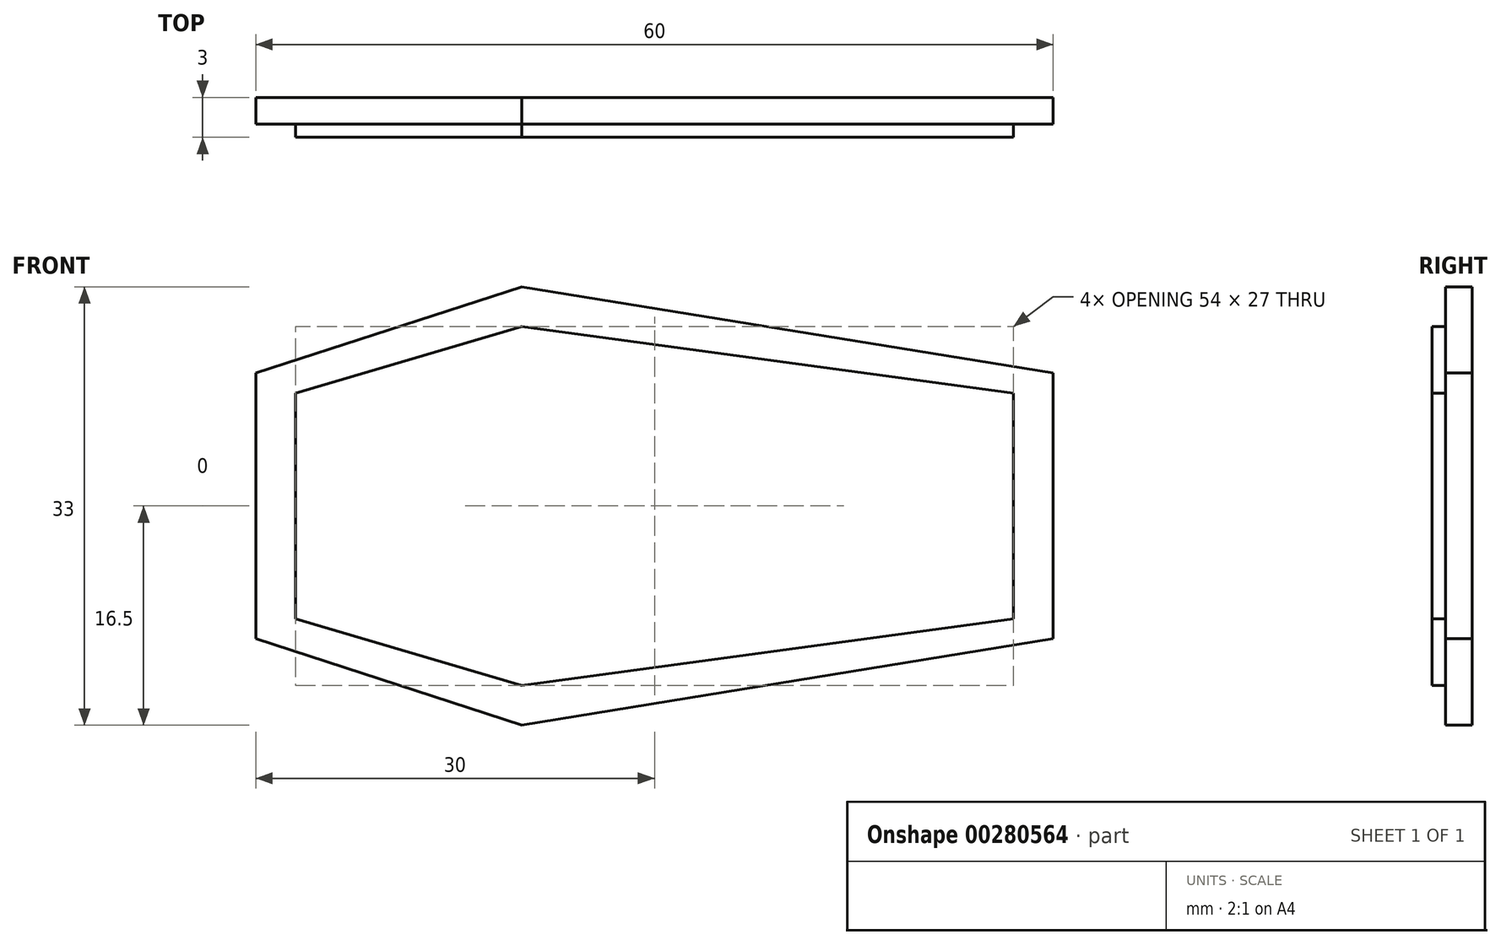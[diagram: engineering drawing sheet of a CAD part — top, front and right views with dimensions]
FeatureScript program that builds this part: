
annotation { "Feature Type Name" : "Feature", "Feature Type Description" : "" }
export const myFeature = defineFeature(function(context is Context, id is Id, definition is map)
    precondition{}
    {
        {
            var Q0;
            Q0=qCreatedBy(makeId("Front.planeOp"),FACE);
            var sketch = newSketch(context, id + "F0", { "sketchPlane" : qUnion([Q0])});
            skLineSegment(sketch, "E0.bottom", {"start": v(30, -10) * mm, "end": v(-30, -10) * mm});
            skLineSegment(sketch, "E0.top", {"start": v(30, 10) * mm, "end": v(-30, 10) * mm});
            skLineSegment(sketch, "E0.left", {"start": v(30, -10) * mm, "end": v(30, 10) * mm});
            skLineSegment(sketch, "E0.right", {"start": v(-30, -10) * mm, "end": v(-30, 10) * mm});
            skPoint(sketch, "E0.middle", {"position": v(0, 0) * mm});
            skPoint(sketch, "E1", {"position": v(-10, 16.5) * mm});
            skPoint(sketch, "E2", {"position": v(-10, -16.5) * mm});
            skLineSegment(sketch, "E3", {"start": v(-10, 16.5) * mm, "end": v(-10, -16.5) * mm});
            skLineSegment(sketch, "E4", {"start": v(-30, -10) * mm, "end": v(-10, -16.5) * mm});
            skLineSegment(sketch, "E5", {"start": v(-30, 10) * mm, "end": v(-10, 16.5) * mm});
            skLineSegment(sketch, "E6", {"start": v(30, 10) * mm, "end": v(-10, 16.5) * mm});
            skLineSegment(sketch, "E7", {"start": v(-10, -16.5) * mm, "end": v(30, -10) * mm});
            skSolve(sketch);
        }
        {
            var Q0;
            {var subQ0=sQuery(id+"F0.wireOp",EDGE,"E0.right");Q0=makeQuery(id+"F0.imprint","IMPRINT",FACE,{"disambiguationData":[TD([[makeQuery(id+"F0.imprint","IMPRINT",EDGE,{"derivedFrom":subQ0}),-1.0]])]});}
            var Q1;
            {var subQ0=sQuery(id+"F0.wireOp",EDGE,"E5");Q1=makeQuery(id+"F0.imprint","IMPRINT",FACE,{"disambiguationData":[TD([[makeQuery(id+"F0.imprint","IMPRINT",EDGE,{"derivedFrom":subQ0}),-1.0]])]});}
            var Q2;
            {var subQ0=sQuery(id+"F0.wireOp",EDGE,"E6");Q2=makeQuery(id+"F0.imprint","IMPRINT",FACE,{"disambiguationData":[TD([[makeQuery(id+"F0.imprint","IMPRINT",EDGE,{"derivedFrom":subQ0}),1.0]])]});}
            var Q3;
            {var subQ0=sQuery(id+"F0.wireOp",EDGE,"E0.left");Q3=makeQuery(id+"F0.imprint","IMPRINT",FACE,{"disambiguationData":[TD([[makeQuery(id+"F0.imprint","IMPRINT",EDGE,{"derivedFrom":subQ0}),1.0]])]});}
            var Q4;
            {var subQ0=sQuery(id+"F0.wireOp",EDGE,"E7");Q4=makeQuery(id+"F0.imprint","IMPRINT",FACE,{"disambiguationData":[TD([[makeQuery(id+"F0.imprint","IMPRINT",EDGE,{"derivedFrom":subQ0}),1.0]])]});}
            var Q5;
            {var subQ0=sQuery(id+"F0.wireOp",EDGE,"E4");Q5=makeQuery(id+"F0.imprint","IMPRINT",FACE,{"disambiguationData":[TD([[makeQuery(id+"F0.imprint","IMPRINT",EDGE,{"derivedFrom":subQ0}),1.0]])]});}
            extrude(context, id + "F1", {"entities" : qUnion([Q0, Q1, Q2, Q3, Q4, Q5]), "depth" : 3 * mm});
        }
        {
            var Q0;
            Q0=makeQuery(id+"F1.opExtrude","CAP_FACE",FACE,{"disambiguationData":[OSD([sQuery(id+"F0.wireOp",EDGE,"E0.left"),sQuery(id+"F0.wireOp",EDGE,"E0.right"),sQuery(id+"F0.wireOp",EDGE,"E4"),sQuery(id+"F0.wireOp",EDGE,"E5"),sQuery(id+"F0.wireOp",EDGE,"E6"),sQuery(id+"F0.wireOp",EDGE,"E7")])],"isStart":false});
            var sketch = newSketch(context, id + "F2", { "sketchPlane" : qUnion([Q0])});
            skLineSegment(sketch, "E8.bottom", {"start": v(27, -8.5) * mm, "end": v(-27, -8.5) * mm});
            skLineSegment(sketch, "E8.top", {"start": v(27, 8.5) * mm, "end": v(-27, 8.5) * mm});
            skLineSegment(sketch, "E8.left", {"start": v(27, -8.5) * mm, "end": v(27, 8.5) * mm});
            skLineSegment(sketch, "E8.right", {"start": v(-27, -8.5) * mm, "end": v(-27, 8.5) * mm});
            skPoint(sketch, "E8.middle", {"position": v(0, 0) * mm});
            skLineSegment(sketch, "E9", {"start": v(-10, 16.5) * mm, "end": v(-10, -16.5) * mm});
            skPoint(sketch, "E10", {"position": v(-10, 13.5) * mm});
            skPoint(sketch, "E11", {"position": v(-10, -13.5) * mm});
            skLineSegment(sketch, "E12", {"start": v(-27, 8.5) * mm, "end": v(-10, 13.5) * mm});
            skLineSegment(sketch, "E13", {"start": v(-27, -8.5) * mm, "end": v(-10, -13.5) * mm});
            skLineSegment(sketch, "E14", {"start": v(-10, 13.5) * mm, "end": v(27, 8.5) * mm});
            skLineSegment(sketch, "E15", {"start": v(-10, -13.5) * mm, "end": v(27, -8.5) * mm});
            skSolve(sketch);
        }
        {
            var Q0;
            Q0=makeQuery(id+"F2.imprint","IMPRINT",FACE,{"disambiguationData":[TD([[makeQuery(id+"F2.imprint","IMPRINT",EDGE,{"derivedFrom":sQuery(id+"F2.wireOp",EDGE,"E8.right")}),1.0]])]});
            var Q1;
            Q1=makeQuery(id+"F2.imprint","IMPRINT",FACE,{"disambiguationData":[TD([[makeQuery(id+"F2.imprint","IMPRINT",EDGE,{"derivedFrom":sQuery(id+"F2.wireOp",EDGE,"E8.left")}),-1.0]])]});
            extrude(context, id + "F3", {"entities" : qUnion([Q0, Q1]), "operationType" : NewBodyOperationType.REMOVE, "oppositeDirection" : true, "depth" : 1 * mm});
        }
    });
